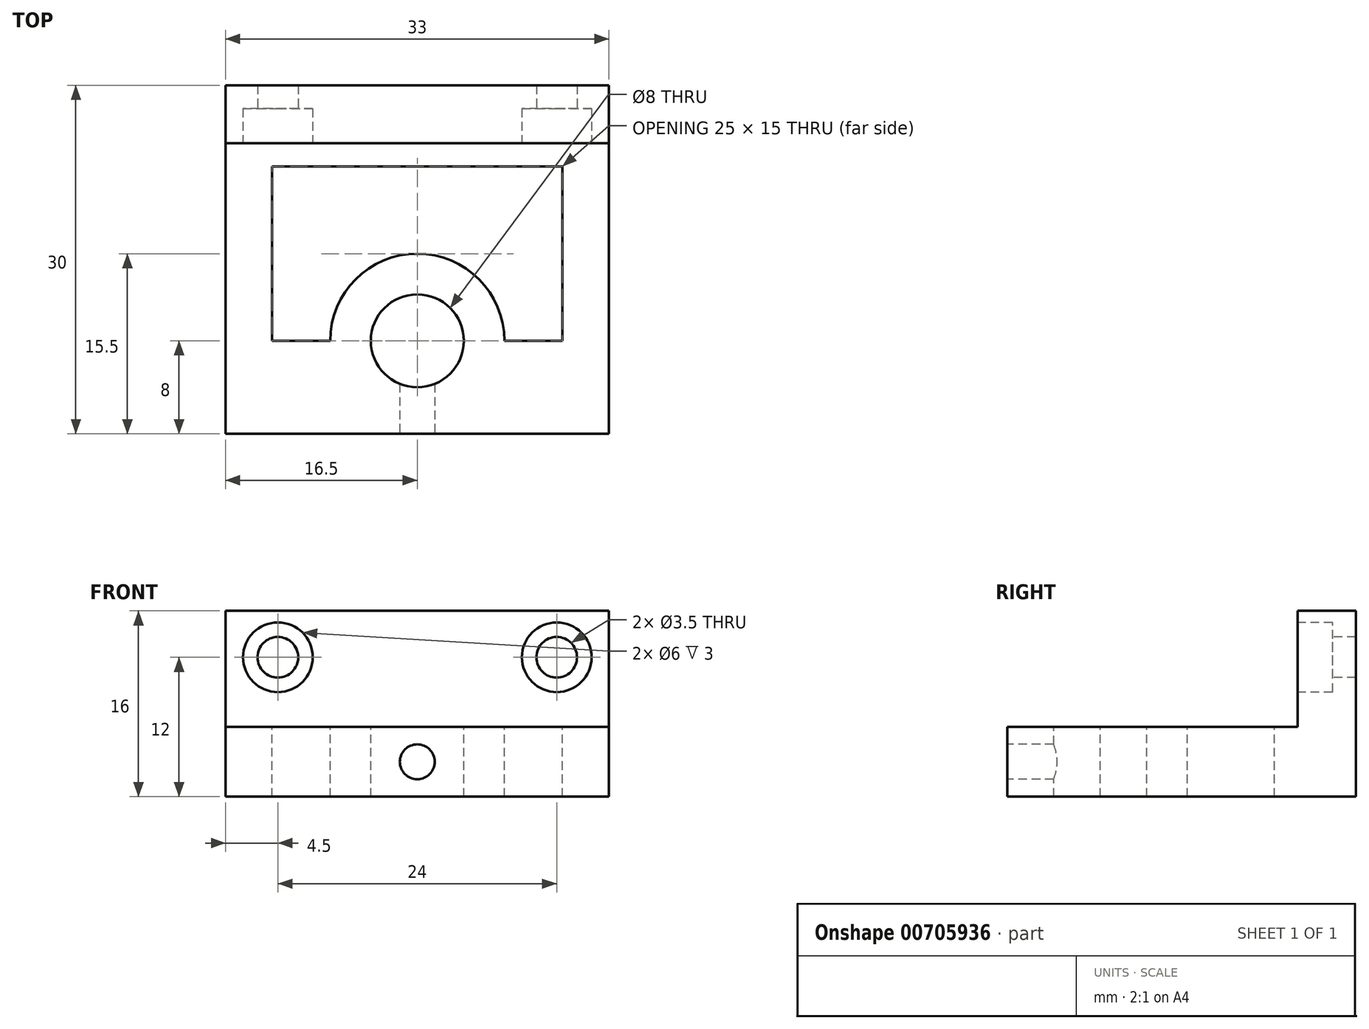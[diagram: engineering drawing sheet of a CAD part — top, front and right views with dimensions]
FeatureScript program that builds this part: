
annotation { "Feature Type Name" : "Feature", "Feature Type Description" : "" }
export const myFeature = defineFeature(function(context is Context, id is Id, definition is map)
    precondition{}
    {
        {
            var Q0;
            Q0=qCreatedBy(makeId("Front.planeOp"),FACE);
            var sketch = newSketch(context, id + "F0", { "sketchPlane" : qUnion([Q0])});
            skLineSegment(sketch, "E0.bottom", {"start": v(16.5, 5) * mm, "end": v(-16.5, 5) * mm});
            skLineSegment(sketch, "E0.top", {"start": v(16.5, -5) * mm, "end": v(-16.5, -5) * mm});
            skLineSegment(sketch, "E0.left", {"start": v(16.5, 5) * mm, "end": v(16.5, -5) * mm});
            skLineSegment(sketch, "E0.right", {"start": v(-16.5, 5) * mm, "end": v(-16.5, -5) * mm});
            skPoint(sketch, "E0.middle", {"position": v(0, 0) * mm});
            skSolve(sketch);
        }
        {
            var Q0;
            Q0=makeQuery(id+"F0.imprint","IMPRINT",FACE,{"disambiguationData":[TD([[makeQuery(id+"F0.imprint","IMPRINT",EDGE,{"derivedFrom":sQuery(id+"F0.wireOp",EDGE,"E0.bottom")}),1.0]])]});
            extrude(context, id + "F1", {"entities" : qUnion([Q0]), "depth" : 5 * mm, "offsetDistance" : 25 * mm});
        }
        {
            var Q0;
            Q0=makeQuery(id+"F1.opExtrude","CAP_FACE",FACE,{"disambiguationData":[OSD([sQuery(id+"F0.wireOp",EDGE,"E0.bottom"),sQuery(id+"F0.wireOp",EDGE,"E0.top"),sQuery(id+"F0.wireOp",EDGE,"E0.left"),sQuery(id+"F0.wireOp",EDGE,"E0.right")])],"isStart":false});
            var sketch = newSketch(context, id + "F2", { "sketchPlane" : qUnion([Q0])});
            skLineSegment(sketch, "E1", {"start": v(-16.5, 1) * mm, "end": v(16.5, 1) * mm, "construction": true});
            skCircle(sketch, "E2", {"center": v(-12, 1) * mm, "radius": 1.75 * mm});
            skCircle(sketch, "E3", {"center": v(12, 1) * mm, "radius": 1.75 * mm});
            skLineSegment(sketch, "E4", {"start": v(0, 0) * mm, "end": v(0, 8.72) * mm, "construction": true});
            skCircle(sketch, "E5", {"center": v(-12, 1) * mm, "radius": 3 * mm});
            skCircle(sketch, "E6", {"center": v(12, 1) * mm, "radius": 3 * mm});
            skSolve(sketch);
        }
        {
            var Q0;
            Q0=makeQuery(id+"F2.imprint","IMPRINT",FACE,{"disambiguationData":[TD([[makeQuery(id+"F2.imprint","IMPRINT",EDGE,{"derivedFrom":sQuery(id+"F2.wireOp",EDGE,"E2")}),1.0]])]});
            var Q1;
            Q1=makeQuery(id+"F2.imprint","IMPRINT",FACE,{"disambiguationData":[TD([[makeQuery(id+"F2.imprint","IMPRINT",EDGE,{"derivedFrom":sQuery(id+"F2.wireOp",EDGE,"E3")}),1.0]])]});
            var Q2;
            Q2=sQuery(id+"F2.wireOp",EDGE,"E2");
            var Q3;
            Q3=sQuery(id+"F2.wireOp",EDGE,"E3");
            extrude(context, id + "F3", {"entities" : qUnion([Q0, Q1]), "operationType" : NewBodyOperationType.REMOVE, "surfaceEntities" : qUnion([Q2, Q3]), "endBound" : BoundingType.UP_TO_NEXT, "oppositeDirection" : true, "depth" : 25 * mm, "offsetDistance" : 25 * mm});
        }
        {
            var Q0;
            Q0=makeQuery(id+"F2.imprint","IMPRINT",FACE,{"disambiguationData":[TD([[makeQuery(id+"F2.imprint","IMPRINT",EDGE,{"derivedFrom":sQuery(id+"F2.wireOp",EDGE,"E2")}),-1.0]])]});
            var Q1;
            Q1=makeQuery(id+"F2.imprint","IMPRINT",FACE,{"disambiguationData":[TD([[makeQuery(id+"F2.imprint","IMPRINT",EDGE,{"derivedFrom":sQuery(id+"F2.wireOp",EDGE,"E3")}),-1.0]])]});
            extrude(context, id + "F4", {"entities" : qUnion([Q0, Q1]), "operationType" : NewBodyOperationType.REMOVE, "oppositeDirection" : true, "depth" : 3 * mm, "offsetDistance" : 25 * mm});
        }
        {
            var Q0;
            Q0=makeQuery(id+"F1.opExtrude","SWEPT_FACE",FACE,{"disambiguationData":[OSD([sQuery(id+"F0.wireOp",EDGE,"E0.top")])]});
            var sketch = newSketch(context, id + "F5", { "sketchPlane" : qUnion([Q0])});
            skLineSegment(sketch, "E7.bottom", {"start": v(-16.5, 0) * mm, "end": v(16.5, 0) * mm});
            skLineSegment(sketch, "E7.top", {"start": v(-16.5, 30) * mm, "end": v(16.5, 30) * mm});
            skLineSegment(sketch, "E7.left", {"start": v(-16.5, 0) * mm, "end": v(-16.5, 30) * mm});
            skLineSegment(sketch, "E7.right", {"start": v(16.5, 0) * mm, "end": v(16.5, 30) * mm});
            skSolve(sketch);
        }
        {
            var Q0;
            Q0 = qSketchRegion(id + "F5", true);
            extrude(context, id + "F6", {"entities" : qUnion([Q0]), "operationType" : NewBodyOperationType.ADD, "depth" : 6 * mm, "offsetDistance" : 25 * mm});
        }
        {
            var Q0;
            Q0=makeQuery(id+"F6.opExtrude","CAP_FACE",FACE,{"disambiguationData":[OSD([sQuery(id+"F5.wireOp",EDGE,"E7.bottom"),sQuery(id+"F5.wireOp",EDGE,"E7.top"),sQuery(id+"F5.wireOp",EDGE,"E7.left"),sQuery(id+"F5.wireOp",EDGE,"E7.right")])],"isStart":true});
            var sketch = newSketch(context, id + "F7", { "sketchPlane" : qUnion([Q0])});
            skLineSegment(sketch, "E8", {"start": v(0, 0) * mm, "end": v(0, -30) * mm, "construction": true});
            skCircle(sketch, "E9", {"center": v(0, -22) * mm, "radius": 4 * mm});
            skSolve(sketch);
        }
        {
            var Q0;
            Q0=makeQuery(id+"F7.imprint","IMPRINT",FACE,{"disambiguationData":[TD([[makeQuery(id+"F7.imprint","IMPRINT",EDGE,{"derivedFrom":sQuery(id+"F7.wireOp",EDGE,"E9")}),1.0]])]});
            var Q1;
            Q1=sQuery(id+"F7.wireOp",EDGE,"E9");
            extrude(context, id + "F8", {"entities" : qUnion([Q0]), "operationType" : NewBodyOperationType.REMOVE, "surfaceEntities" : qUnion([Q1]), "endBound" : BoundingType.UP_TO_NEXT, "oppositeDirection" : true, "depth" : 25 * mm, "offsetDistance" : 25 * mm});
        }
        {
            var Q0;
            Q0=makeQuery(id+"F6.opExtrude","SWEPT_FACE",FACE,{"disambiguationData":[OSD([sQuery(id+"F5.wireOp",EDGE,"E7.top")])]});
            var sketch = newSketch(context, id + "F9", { "sketchPlane" : qUnion([Q0])});
            skLineSegment(sketch, "E10", {"start": v(0, 0) * mm, "end": v(0, -11) * mm, "construction": true});
            skCircle(sketch, "E11", {"center": v(0, -8) * mm, "radius": 1.5 * mm});
            skSolve(sketch);
        }
        {
            var Q0;
            Q0 = qSketchRegion(id + "F9", true);
            extrude(context, id + "F10", {"entities" : qUnion([Q0]), "operationType" : NewBodyOperationType.REMOVE, "endBound" : BoundingType.UP_TO_NEXT, "oppositeDirection" : true, "depth" : 25 * mm, "offsetDistance" : 25 * mm});
        }
        {
            var Q0;
            Q0=makeQuery(id+"F6.opExtrude","CAP_FACE",FACE,{"disambiguationData":[OSD([sQuery(id+"F5.wireOp",EDGE,"E7.bottom"),sQuery(id+"F5.wireOp",EDGE,"E7.top"),sQuery(id+"F5.wireOp",EDGE,"E7.left"),sQuery(id+"F5.wireOp",EDGE,"E7.right")])],"isStart":true});
            var sketch = newSketch(context, id + "F11", { "sketchPlane" : qUnion([Q0])});
            skLineSegment(sketch, "E12.top", {"start": v(-12.5, -7) * mm, "end": v(12.5, -7) * mm});
            skLineSegment(sketch, "E12.left", {"start": v(-12.5, -14.66) * mm, "end": v(-12.5, -7) * mm});
            skLineSegment(sketch, "E12.right", {"start": v(12.5, -14.66) * mm, "end": v(12.5, -7) * mm});
            skArc(sketch, "E13", {"start": v(7.5, -22) * mm, "mid": v(0, -14.5) * mm, "end": v(-7.5, -22) * mm});
            skLineSegment(sketch, "E14", {"start": v(12.5, -14.66) * mm, "end": v(12.5, -22) * mm});
            skLineSegment(sketch, "E15", {"start": v(-12.5, -14.66) * mm, "end": v(-12.5, -22) * mm});
            skLineSegment(sketch, "E16", {"start": v(-12.5, -22) * mm, "end": v(-7.5, -22) * mm});
            skLineSegment(sketch, "E17.trimOffspring", {"start": v(7.5, -22) * mm, "end": v(12.5, -22) * mm});
            skSolve(sketch);
        }
        {
            var Q0;
            Q0 = qSketchRegion(id + "F11", true);
            extrude(context, id + "F12", {"entities" : qUnion([Q0]), "operationType" : NewBodyOperationType.REMOVE, "endBound" : BoundingType.UP_TO_NEXT, "oppositeDirection" : true, "depth" : 25 * mm, "offsetDistance" : 25 * mm});
        }
    });
